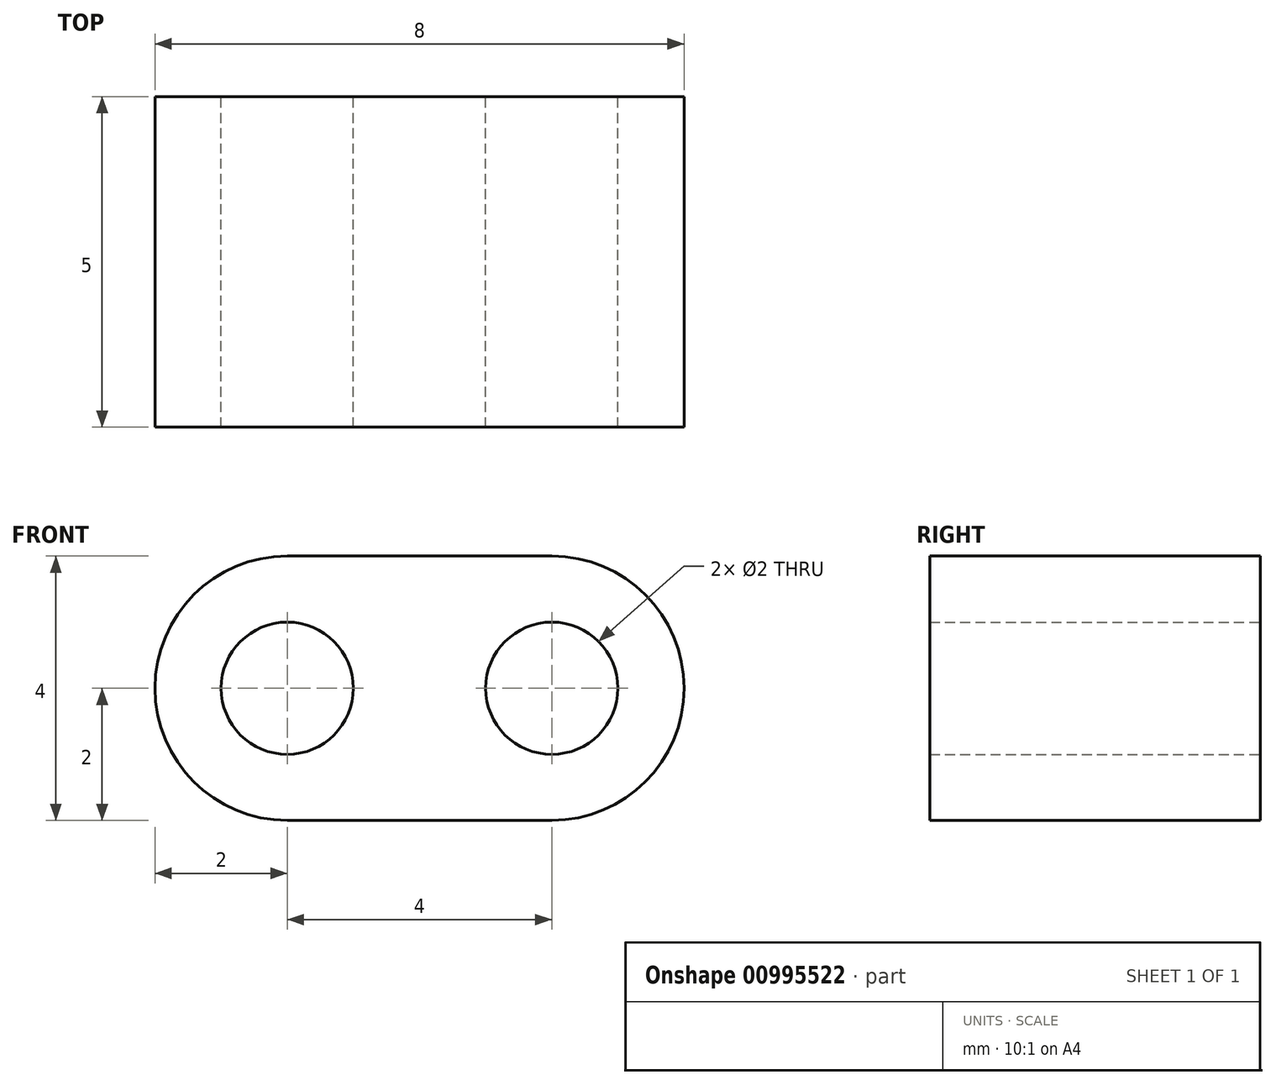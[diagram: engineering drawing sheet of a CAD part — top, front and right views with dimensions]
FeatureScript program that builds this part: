
annotation { "Feature Type Name" : "Feature", "Feature Type Description" : "" }
export const myFeature = defineFeature(function(context is Context, id is Id, definition is map)
    precondition{}
    {
        {
            var Q0;
            Q0=qCreatedBy(makeId("Front.planeOp"),FACE);
            var sketch = newSketch(context, id + "F0", { "sketchPlane" : qUnion([Q0])});
            skCircle(sketch, "E0", {"center": v(0, 0) * mm, "radius": 1 * mm});
            skArc(sketch, "E1", {"start": v(0, -2) * mm, "mid": v(2, 0) * mm, "end": v(0, 2) * mm});
            skLineSegment(sketch, "E2", {"start": v(0, 2) * mm, "end": v(-4, 2) * mm});
            skArc(sketch, "E3", {"start": v(-4, 2) * mm, "mid": v(-6, 0) * mm, "end": v(-4, -2) * mm});
            skCircle(sketch, "E4", {"center": v(-4, 0) * mm, "radius": 1 * mm});
            skLineSegment(sketch, "E5", {"start": v(0, -2) * mm, "end": v(-4, -2) * mm});
            skPoint(sketch, "E6.orphan", {"position": v(-2, 0) * mm});
            skSolve(sketch);
        }
        {
            var Q0;
            Q0 = qSketchRegion(id + "F0", true);
            extrude(context, id + "F1", {"entities" : qUnion([Q0]), "depth" : 5 * mm, "offsetDistance" : 25 * mm});
        }
    });
